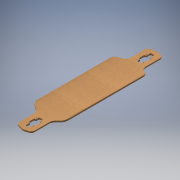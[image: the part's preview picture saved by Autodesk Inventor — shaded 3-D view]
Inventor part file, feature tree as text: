
AUTODESK INVENTOR PART (.ipt)
format: ipt  version: 2016 (Build 200138000, 138)  size: 614,400 bytes
history: native  units: in
note: dims shown in document units (in); Inventor stores cm internally (conversion verified against a paired STEP export)
features: fillet x6, extrude x4, sketch x4, plane x2, mirror x1, other x1
ambient origin geometry x8: Origin, YZ Plane, XZ Plane, XY Plane, X Axis, Y Axis, Z Axis, Center Point
bodies: Solid1 (feature_tree), Solid2 (feature_tree)
feature tree (18):
  extrude  "Extrusion1"  Depth=4.5in
  fillet  "Fillet1"  [1 undecoded]
  fillet  "Fillet2"  [1 undecoded]
  fillet  "Fillet3"  Radius=6.0in
  fillet  "Fillet4"  Radius=1.1in
  fillet  "Fillet5"  Radius=1.375in
  mirror  "Mirror1"
  extrude  "Extrusion3"  Depth=2.0in
  fillet  "Fillet6"  Radius=1.4in
  plane  "Work Plane1"
  extrude  "Extrusion4"  Depth=1.625in
  plane  "Work Plane2"
  extrude  "Extrusion5"  Depth=0.5in
  sketch  "Sketch1"  dims[d12=40.0in d20=4.5in d22=75.0deg d29=120.0deg d30=6.0in d31=1.1in d33=1.375in]
  other  "Image1"
  sketch  "Sketch3"  dims[d34=4.125in d36=2.0in d37=1.4in]
  sketch  "Sketch4"  dims[d38=1.0in d40=1.625in]
  sketch  "Sketch5"  dims[d42=0.21in d43=1.625in d45=2.5in d46=0.325in d49=4.0in d50=0.0in d51=1.0in d52=1.75in d60=9.5in d64=0.25in d65=0.125in d66=1.5in d67=0.475in d96=1.125in d98=0.475in d100=0.0in d101=0.0in d102=0.125in d103=100.0in d104=0.0in d105=0.0in d106=0.1378in d108=0.5in d109=0.0in d110=0.0in d111=1.02in d112=0.58in]
note: 2 required parameter values undecoded (feature->parameter linkage not recoverable at this tier; creation-order binding heuristic only, values carry confidence <= 0.55)
